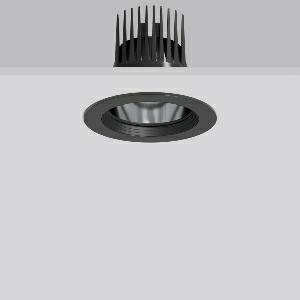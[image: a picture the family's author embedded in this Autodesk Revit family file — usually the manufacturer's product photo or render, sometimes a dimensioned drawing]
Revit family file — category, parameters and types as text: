
# Revit family: heledon_maxi_e_901757_003_449b
name_source: partatom
category: Lighting Fixtures
units: mm (PartAtom-declared; Revit-internal decimal feet)

## family parameters
Cut with Voids When Loaded = No
Host = Face
Light Source = No
Part Type = Normal
Room Calculation Point = No
Round Connector Dimension = Use Diameter
Shared = No

## types (1)
- HELEDON maxi E (1 x LED Modul 930, 3350 lm, 3000)
    Apparent Load = 25 VA
    Approval mark = CE
    CIE Flux Codes = 100 100 100 100 100
    Color Rendering = 90
    Color Temperature = 3000
    Default Elevation = 1800 mm
    Description = Series: HELEDON maxi
Round recessed downlight. Housing: die-cast aluminium, powder-coated. Black plastic ring and recessed LED to prevent glare from the side. Optical assembly with reflector made of MIRO-Silver with 98% total light reflection for outstanding efficiency - can be changed without tools. Best colour rendering index Ra>90. Suitable for Recessed ceiling mounting. Installation without tools thanks to spring fastening system. Including separate LED converter with connecting cable 600 mm.High quality converter without flickering and stroboscopic effect. Through-wiring box (5 pole) available as accessory. The following accessories can be mounted without use of tools: interchangeable lenses, decorative glasses, honeycomb louvre, clear and frosted diffusers, white interchangeable plastic ring. 
Colour: deep black, matt (RAL 9005)
Diameter: 162 mm
Height: 3 mm
Cut-out diameter: 152 mm
Recess height: 200 mm
Luminaire: recess height: 135 mm
Lamp: LED
Socket: without socket
Colour temperature: 3000K
Colour rendering index (CRI): 92
System power: 25 W
Rated luminous flux: 3350 lm
Luminous efficiency: 134 lm/W
Control gear: Regulated power supply
Protection class: II
Type of protection: IP 20
    Height = 0 mm  [stored 0 ft]
    Lamp = 1 x LED Modul 930
    Lamp Light Flux = 3350 lm
    Lamp count = 1
    Length = 162 mm
    Lifetime = 50000 h
    Luminous efficacy = 134 lm/W
    Manufacturer = RZB
    ModVariant = No
    Model = 901757.003
    Mounting Place = Ceiling
    Mounting Type = Recessed
    Number of Poles = 1
    OnlyDefault = Yes
    Power Factor = 1
    Product Name = HELEDON maxi E
    Product group = Recessed downlights
    ProductGroupID = 402
    Protection Class = Protection class II
    Protection Degree = IP 20
    RLX_Detail_Level = 1
    RLX_Emergency_Light_Flux = 0 lm
    RLX_Emergency_Type = 0
    RLX_Emergency_Type_DB = No
    RlxData = <blob elided: 120297 chars, md5=d87ab4d5>
    Socket = socket
    Standby Power = 0 W
    System Light Flux = 3350 lm
    System Power = 25 W
    Type Comments = Product without accessories
    Type Image = 901662.003.jpg
    URL = http://relux.com
    VarID = ---
    Voltage = 230 V
    Voltage Range = 220-240 V
    Weight = 0.00 kg
    Width = 0 mm  [stored 0 ft]

note: [stored X ft] marks values corroborated as IEEE doubles in the binary element streams (Revit-internal decimal feet)

## geometry (parser evidence)
native form markers: Blend x4, Sweep x11
no freeform markers — native parametric forms only
